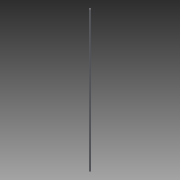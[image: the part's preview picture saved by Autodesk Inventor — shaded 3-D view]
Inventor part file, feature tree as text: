
AUTODESK INVENTOR PART (.ipt)
format: ipt  version: 2015 SP1 (Build 190203100, 203)  size: 62,976 bytes
history: native  units: in
note: dims shown in document units (in); Inventor stores cm internally (conversion verified against a paired STEP export)
features: extrude x1, sketch x1
ambient origin geometry x8: Origin, YZ Plane, XZ Plane, XY Plane, X Axis, Y Axis, Z Axis, Center Point
bodies: Solid1 (feature_tree)
feature tree (2):
  extrude  "Extrusion1"  Depth=14.0in TaperAngle=0.0deg
  sketch  "Sketch1"  dims[d0=0.125in d1=14.0in d2=0.0in]
